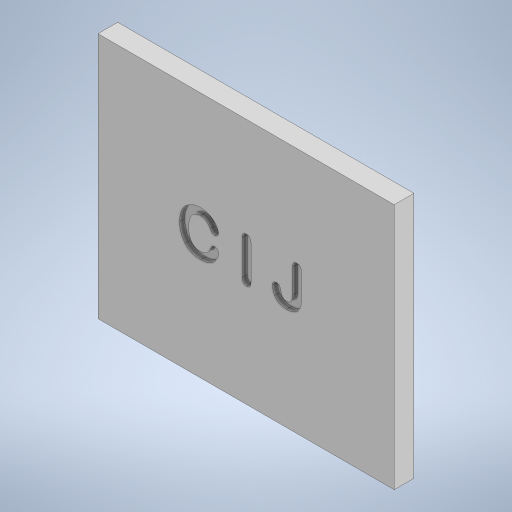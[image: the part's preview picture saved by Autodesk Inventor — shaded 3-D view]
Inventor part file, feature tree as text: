
AUTODESK INVENTOR PART (.ipt)
format: ipt  version: 2023 (Build 270158000, 158)  size: 251,904 bytes
history: native  units: mm
features: extrude x2, sketch x2, other x1
ambient origin geometry x8: Origin, YZ Plane, XZ Plane, XY Plane, X Axis, Y Axis, Z Axis, Center Point
bodies: Body1 (feature_tree)
feature tree (5):
  other  "Sólido1"
  extrude  "Extrusión1"  Depth=250.0mm
  extrude  "Extrusión2"  Depth=5.0mm TaperAngle=0.0deg
  sketch  "Boceto1"  dims[d0=300.0mm d1=250.0mm]
  sketch  "Boceto2"  dims[d2=20.0mm d3=0.0mm d4=5.0mm d5=0.0mm]
